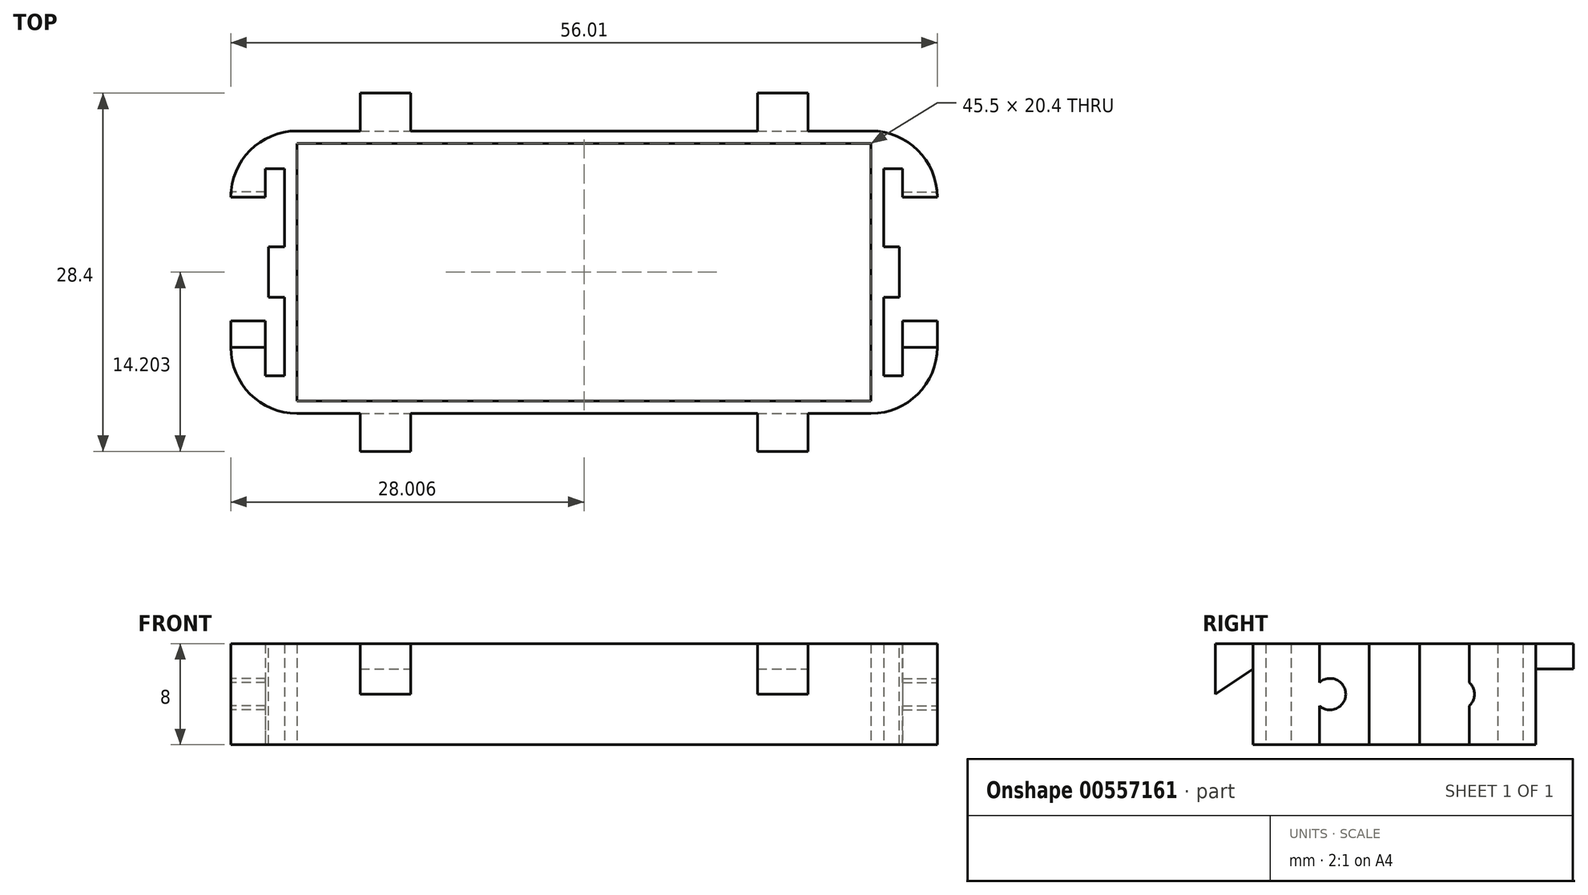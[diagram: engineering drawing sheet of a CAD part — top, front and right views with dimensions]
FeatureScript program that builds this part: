
annotation { "Feature Type Name" : "Feature", "Feature Type Description" : "" }
export const myFeature = defineFeature(function(context is Context, id is Id, definition is map)
    precondition{}
    {
        {
            var Q0;
            Q0=qCreatedBy(makeId("Top.planeOp"),FACE);
            var sketch = newSketch(context, id + "F0", { "sketchPlane" : qUnion([Q0])});
            skLineSegment(sketch, "E0.right", {"start": v(-56.91, 31.47) * mm, "end": v(-56.91, 37.67) * mm});
            skLineSegment(sketch, "E1.right", {"start": v(-58.41, 31.47) * mm, "end": v(-58.41, 37.67) * mm});
            skLineSegment(sketch, "E2", {"start": v(-58.41, 47.87) * mm, "end": v(-56.91, 47.87) * mm});
            skLineSegment(sketch, "E3", {"start": v(-58.41, 41.67) * mm, "end": v(-56.91, 41.67) * mm});
            skLineSegment(sketch, "E4.MirrorCS", {"start": v(-58.41, 31.47) * mm, "end": v(-56.91, 31.47) * mm});
            skLineSegment(sketch, "E5.MirrorCS", {"start": v(-58.41, 37.67) * mm, "end": v(-56.91, 37.67) * mm});
            skLineSegment(sketch, "E6.trimOffspring", {"start": v(-58.41, 41.67) * mm, "end": v(-58.41, 47.87) * mm});
            skLineSegment(sketch, "E7.trimOffspring", {"start": v(-56.91, 41.67) * mm, "end": v(-56.91, 47.87) * mm});
            skPoint(sketch, "E8", {"position": v(-55.91, 39.67) * mm});
            skPoint(sketch, "E9", {"position": v(-58.41, 44.77) * mm});
            skPoint(sketch, "E10", {"position": v(-58.41, 34.57) * mm});
            skPoint(sketch, "E11", {"position": v(-55.91, 50.87) * mm});
            skPoint(sketch, "E12", {"position": v(-55.91, 28.47) * mm});
            skArc(sketch, "E13", {"start": v(-55.91, 50.87) * mm, "mid": v(-59.63, 49.33) * mm, "end": v(-61.17, 45.62) * mm});
            skArc(sketch, "E14.MirrorCS", {"start": v(-55.91, 28.47) * mm, "mid": v(-59.63, 30.01) * mm, "end": v(-61.17, 33.72) * mm});
            skLineSegment(sketch, "E15", {"start": v(-61.17, 33.72) * mm, "end": v(-61.17, 45.62) * mm});
            skLineSegment(sketch, "E16.MirrorCS", {"start": v(-7.91, 37.67) * mm, "end": v(-9.41, 37.67) * mm});
            skLineSegment(sketch, "E17.MirrorCS", {"start": v(-7.91, 31.47) * mm, "end": v(-9.41, 31.47) * mm});
            skLineSegment(sketch, "E18.MirrorCS", {"start": v(-7.91, 41.67) * mm, "end": v(-9.41, 41.67) * mm});
            skLineSegment(sketch, "E19.MirrorCS", {"start": v(-7.91, 47.87) * mm, "end": v(-9.41, 47.87) * mm});
            skLineSegment(sketch, "E20.MirrorCS", {"start": v(-9.41, 31.47) * mm, "end": v(-9.41, 37.67) * mm});
            skLineSegment(sketch, "E21.MirrorCS", {"start": v(-9.41, 41.67) * mm, "end": v(-9.41, 47.87) * mm});
            skLineSegment(sketch, "E22.MirrorCS", {"start": v(-7.91, 41.67) * mm, "end": v(-7.91, 47.87) * mm});
            skLineSegment(sketch, "E23.MirrorCS", {"start": v(-7.91, 31.47) * mm, "end": v(-7.91, 37.67) * mm});
            skLineSegment(sketch, "E24.MirrorCS", {"start": v(-5.16, 33.72) * mm, "end": v(-5.16, 45.62) * mm});
            skPoint(sketch, "E25.MirrorP", {"position": v(-7.91, 34.57) * mm});
            skArc(sketch, "E26.MirrorCS", {"start": v(-10.41, 50.87) * mm, "mid": v(-6.7, 49.33) * mm, "end": v(-5.16, 45.62) * mm});
            skPoint(sketch, "E27.MirrorP", {"position": v(-10.41, 28.47) * mm});
            skPoint(sketch, "E28.MirrorP", {"position": v(-10.41, 39.67) * mm});
            skArc(sketch, "E29.MirrorCS", {"start": v(-10.41, 28.47) * mm, "mid": v(-6.7, 30.01) * mm, "end": v(-5.16, 33.72) * mm});
            skPoint(sketch, "E30.MirrorP", {"position": v(-7.91, 44.77) * mm});
            skPoint(sketch, "E31.MirrorP", {"position": v(-10.41, 50.87) * mm});
            skLineSegment(sketch, "E32", {"start": v(-55.91, 49.87) * mm, "end": v(-10.41, 49.87) * mm});
            skLineSegment(sketch, "E33", {"start": v(-55.91, 50.87) * mm, "end": v(-10.41, 50.87) * mm});
            skLineSegment(sketch, "E34", {"start": v(-55.91, 29.47) * mm, "end": v(-10.41, 29.47) * mm});
            skLineSegment(sketch, "E35", {"start": v(-55.91, 28.47) * mm, "end": v(-10.41, 28.47) * mm});
            skText(sketch, "E36", { "text": "AAA Double Holder", "fontName": "Arimo-Italic.ttf"});
            skLineSegment(sketch, "E37", {"start": v(-55.91, 49.87) * mm, "end": v(-55.91, 29.47) * mm});
            skLineSegment(sketch, "E38", {"start": v(-10.41, 49.87) * mm, "end": v(-10.41, 29.47) * mm});
            skPoint(sketch, "E39", {"position": v(-56.91, 44.77) * mm});
            skPoint(sketch, "E40", {"position": v(-61.17, 44.77) * mm});
            skPoint(sketch, "E41", {"position": v(-61.17, 34.57) * mm});
            skPoint(sketch, "E42", {"position": v(-56.91, 34.57) * mm});
            skPoint(sketch, "E43", {"position": v(-55.91, 34.57) * mm});
            skPoint(sketch, "E44", {"position": v(-55.91, 44.77) * mm});
            skPoint(sketch, "E45", {"position": v(-9.41, 44.77) * mm});
            skPoint(sketch, "E46", {"position": v(-10.41, 44.77) * mm});
            skPoint(sketch, "E47", {"position": v(-9.41, 34.57) * mm});
            skPoint(sketch, "E48", {"position": v(-10.41, 34.57) * mm});
            skPoint(sketch, "E49", {"position": v(-5.16, 34.57) * mm});
            skPoint(sketch, "E50", {"position": v(-5.16, 44.77) * mm});
            const initialGuessF0  = {"E36": [-0.0583, 0.057, 1, 0, 0.00408]};
            skSetInitialGuess(sketch, initialGuessF0);
            skSolve(sketch);
        }
        {
            var Q0;
            Q0=makeQuery(id+"F0.imprint","IMPRINT",FACE,{"disambiguationData":[TD([[makeQuery(id+"F0.imprint","IMPRINT",EDGE,{"derivedFrom":sQuery(id+"F0.wireOp",EDGE,"E0.right")}),-1.0]])]});
            extrude(context, id + "F1", {"entities" : qUnion([Q0]), "depth" : 8 * mm, "offsetDistance" : 25 * mm});
        }
        {
            var Q0;
            Q0=makeQuery(id+"F1.opExtrude","SWEPT_FACE",FACE,{"disambiguationData":[OSD([sQuery(id+"F0.wireOp",EDGE,"E24.MirrorCS")])]});
            var sketch = newSketch(context, id + "F2", { "sketchPlane" : qUnion([Q0])});
            skPoint(sketch, "E51.0", {"position": v(44.77, 0) * mm});
            skPoint(sketch, "E51.1", {"position": v(34.57, 0) * mm});
            skPoint(sketch, "E51.2", {"position": v(44.77, 0) * mm});
            skPoint(sketch, "E51.3", {"position": v(34.57, 0) * mm});
            skCircle(sketch, "E52", {"center": v(44.77, 4) * mm, "radius": 1.25 * mm});
            skPoint(sketch, "E52.centerSnap0", {"position": v(45.62, 4) * mm});
            skPoint(sketch, "E53.0", {"position": v(39.67, 0) * mm});
            skLineSegment(sketch, "E54", {"start": v(39.67, 0) * mm, "end": v(39.67, 8) * mm, "construction": true});
            skCircle(sketch, "E55.MirrorC", {"center": v(34.57, 4) * mm, "radius": 1.25 * mm});
            skSolve(sketch);
        }
        {
            var Q0;
            Q0=makeQuery(id+"F1.opExtrude","SWEPT_FACE",FACE,{"disambiguationData":[OSD([sQuery(id+"F0.wireOp",EDGE,"E15")])]});
            var sketch = newSketch(context, id + "F3", { "sketchPlane" : qUnion([Q0])});
            skPoint(sketch, "E56.0", {"position": v(-44.77, 0) * mm});
            skPoint(sketch, "E56.1", {"position": v(-34.57, 0) * mm});
            skPoint(sketch, "E56.2", {"position": v(-39.67, 0) * mm});
            skPoint(sketch, "E57.0", {"position": v(-45.62, 4) * mm});
            skPoint(sketch, "E57.1", {"position": v(-33.72, 4) * mm});
            skCircle(sketch, "E58", {"center": v(-44.77, 4) * mm, "radius": 1.25 * mm});
            skCircle(sketch, "E59.MirrorC", {"center": v(-34.57, 4) * mm, "radius": 1.25 * mm});
            skSolve(sketch);
        }
        {
            var Q0;
            {var subQ0=sQuery(id+"F3.wireOp",EDGE,"E58");var subQ1=makeQuery(id+"F1.opExtrude","SWEPT_EDGE",EDGE,{"disambiguationData":[OSD([sQuery(id+"F0.wireOp",EDGE,"E13"),sQuery(id+"F0.wireOp",EDGE,"E15")])]});var subQ2=makeQuery(id+"F3.imprint","INTERSECT",VERTEX,{"disambiguationData":[OD(0.0)],"derivedFrom":[subQ1,subQ0]});Q0=makeQuery(id+"F3.imprint","IMPRINT",FACE,{"disambiguationData":[TD([[makeQuery(id+"F3.imprint","IMPRINT",EDGE,{"disambiguationData":[TD([[subQ2,-1.0]])],"derivedFrom":subQ0}),1.0]])]});}
            var Q1;
            {var subQ0=sQuery(id+"F3.wireOp",EDGE,"E58");var subQ1=makeQuery(id+"F1.opExtrude","SWEPT_EDGE",EDGE,{"disambiguationData":[OSD([sQuery(id+"F0.wireOp",EDGE,"E13"),sQuery(id+"F0.wireOp",EDGE,"E15")])]});var subQ2=makeQuery(id+"F3.imprint","INTERSECT",VERTEX,{"disambiguationData":[OD(0.0)],"derivedFrom":[subQ1,subQ0]});Q1=makeQuery(id+"F3.imprint","IMPRINT",FACE,{"disambiguationData":[TD([[makeQuery(id+"F3.imprint","IMPRINT",EDGE,{"disambiguationData":[TD([[subQ2,1.0]])],"derivedFrom":subQ0}),1.0]])]});}
            var Q2;
            {var subQ0=sQuery(id+"F3.wireOp",EDGE,"E59.MirrorC");var subQ1=makeQuery(id+"F1.opExtrude","SWEPT_EDGE",EDGE,{"disambiguationData":[OSD([sQuery(id+"F0.wireOp",EDGE,"E14.MirrorCS"),sQuery(id+"F0.wireOp",EDGE,"E15")])]});var subQ2=makeQuery(id+"F3.imprint","INTERSECT",VERTEX,{"disambiguationData":[OD(0.0)],"derivedFrom":[subQ1,subQ0]});Q2=makeQuery(id+"F3.imprint","IMPRINT",FACE,{"disambiguationData":[TD([[makeQuery(id+"F3.imprint","IMPRINT",EDGE,{"disambiguationData":[TD([[subQ2,-1.0]])],"derivedFrom":subQ0}),-1.0]])]});}
            var Q3;
            {var subQ0=sQuery(id+"F3.wireOp",EDGE,"E59.MirrorC");var subQ1=makeQuery(id+"F1.opExtrude","SWEPT_EDGE",EDGE,{"disambiguationData":[OSD([sQuery(id+"F0.wireOp",EDGE,"E14.MirrorCS"),sQuery(id+"F0.wireOp",EDGE,"E15")])]});var subQ2=makeQuery(id+"F3.imprint","INTERSECT",VERTEX,{"disambiguationData":[OD(0.0)],"derivedFrom":[subQ1,subQ0]});Q3=makeQuery(id+"F3.imprint","IMPRINT",FACE,{"disambiguationData":[TD([[makeQuery(id+"F3.imprint","IMPRINT",EDGE,{"disambiguationData":[TD([[subQ2,1.0]])],"derivedFrom":subQ0}),-1.0]])]});}
            extrude(context, id + "F4", {"entities" : qUnion([Q0, Q1, Q2, Q3]), "operationType" : NewBodyOperationType.REMOVE, "oppositeDirection" : true, "depth" : 3 * mm, "offsetDistance" : 25 * mm});
        }
        {
            var Q0;
            {var subQ0=sQuery(id+"F2.wireOp",EDGE,"E55.MirrorC");var subQ1=makeQuery(id+"F1.opExtrude","SWEPT_EDGE",EDGE,{"disambiguationData":[OSD([sQuery(id+"F0.wireOp",EDGE,"E24.MirrorCS"),sQuery(id+"F0.wireOp",EDGE,"E29.MirrorCS")])]});var subQ2=makeQuery(id+"F2.imprint","INTERSECT",VERTEX,{"disambiguationData":[OD(0.0)],"derivedFrom":[subQ1,subQ0]});Q0=makeQuery(id+"F2.imprint","IMPRINT",FACE,{"disambiguationData":[TD([[makeQuery(id+"F2.imprint","IMPRINT",EDGE,{"disambiguationData":[TD([[subQ2,1.0]])],"derivedFrom":subQ0}),-1.0]])]});}
            var Q1;
            {var subQ0=sQuery(id+"F2.wireOp",EDGE,"E52");var subQ1=makeQuery(id+"F1.opExtrude","SWEPT_EDGE",EDGE,{"disambiguationData":[OSD([sQuery(id+"F0.wireOp",EDGE,"E24.MirrorCS"),sQuery(id+"F0.wireOp",EDGE,"E26.MirrorCS")])]});var subQ2=makeQuery(id+"F2.imprint","INTERSECT",VERTEX,{"disambiguationData":[OD(0.0)],"derivedFrom":[subQ1,subQ0]});Q1=makeQuery(id+"F2.imprint","IMPRINT",FACE,{"disambiguationData":[TD([[makeQuery(id+"F2.imprint","IMPRINT",EDGE,{"disambiguationData":[TD([[subQ2,1.0]])],"derivedFrom":subQ0}),1.0]])]});}
            var Q2;
            {var subQ0=sQuery(id+"F2.wireOp",EDGE,"E52");var subQ1=makeQuery(id+"F1.opExtrude","SWEPT_EDGE",EDGE,{"disambiguationData":[OSD([sQuery(id+"F0.wireOp",EDGE,"E24.MirrorCS"),sQuery(id+"F0.wireOp",EDGE,"E26.MirrorCS")])]});var subQ2=makeQuery(id+"F2.imprint","INTERSECT",VERTEX,{"disambiguationData":[OD(0.0)],"derivedFrom":[subQ1,subQ0]});Q2=makeQuery(id+"F2.imprint","IMPRINT",FACE,{"disambiguationData":[TD([[makeQuery(id+"F2.imprint","IMPRINT",EDGE,{"disambiguationData":[TD([[subQ2,-1.0]])],"derivedFrom":subQ0}),1.0]])]});}
            var Q3;
            {var subQ0=sQuery(id+"F2.wireOp",EDGE,"E55.MirrorC");var subQ1=makeQuery(id+"F1.opExtrude","SWEPT_EDGE",EDGE,{"disambiguationData":[OSD([sQuery(id+"F0.wireOp",EDGE,"E24.MirrorCS"),sQuery(id+"F0.wireOp",EDGE,"E29.MirrorCS")])]});var subQ2=makeQuery(id+"F2.imprint","INTERSECT",VERTEX,{"disambiguationData":[OD(0.0)],"derivedFrom":[subQ1,subQ0]});Q3=makeQuery(id+"F2.imprint","IMPRINT",FACE,{"disambiguationData":[TD([[makeQuery(id+"F2.imprint","IMPRINT",EDGE,{"disambiguationData":[TD([[subQ2,-1.0]])],"derivedFrom":subQ0}),-1.0]])]});}
            extrude(context, id + "F5", {"entities" : qUnion([Q0, Q1, Q2, Q3]), "operationType" : NewBodyOperationType.REMOVE, "oppositeDirection" : true, "depth" : 3 * mm, "offsetDistance" : 25 * mm});
        }
        {
            var Q0;
            Q0=makeQuery(id+"F1.opExtrude","CAP_FACE",FACE,{"disambiguationData":[OSD([sQuery(id+"F0.wireOp",EDGE,"E0.right"),sQuery(id+"F0.wireOp",EDGE,"E1.right"),sQuery(id+"F0.wireOp",EDGE,"E2"),sQuery(id+"F0.wireOp",EDGE,"E3"),sQuery(id+"F0.wireOp",EDGE,"E4.MirrorCS"),sQuery(id+"F0.wireOp",EDGE,"E5.MirrorCS"),sQuery(id+"F0.wireOp",EDGE,"E6.trimOffspring"),sQuery(id+"F0.wireOp",EDGE,"E7.trimOffspring"),sQuery(id+"F0.wireOp",EDGE,"E13"),sQuery(id+"F0.wireOp",EDGE,"E14.MirrorCS"),sQuery(id+"F0.wireOp",EDGE,"E15"),sQuery(id+"F0.wireOp",EDGE,"E16.MirrorCS"),sQuery(id+"F0.wireOp",EDGE,"E17.MirrorCS"),sQuery(id+"F0.wireOp",EDGE,"E18.MirrorCS"),sQuery(id+"F0.wireOp",EDGE,"E19.MirrorCS"),sQuery(id+"F0.wireOp",EDGE,"E22.MirrorCS"),sQuery(id+"F0.wireOp",EDGE,"E23.MirrorCS"),sQuery(id+"F0.wireOp",EDGE,"E20.MirrorCS"),sQuery(id+"F0.wireOp",EDGE,"E21.MirrorCS"),sQuery(id+"F0.wireOp",EDGE,"E24.MirrorCS"),sQuery(id+"F0.wireOp",EDGE,"E26.MirrorCS"),sQuery(id+"F0.wireOp",EDGE,"E29.MirrorCS"),sQuery(id+"F0.wireOp",EDGE,"E32"),sQuery(id+"F0.wireOp",EDGE,"E33"),sQuery(id+"F0.wireOp",EDGE,"E34"),sQuery(id+"F0.wireOp",EDGE,"E35"),sQuery(id+"F0.wireOp",EDGE,"E37"),sQuery(id+"F0.wireOp",EDGE,"E38")])],"isStart":false});
            var sketch = newSketch(context, id + "F6", { "sketchPlane" : qUnion([Q0])});
            skPoint(sketch, "E60", {"position": v(-33.16, 50.87) * mm});
            skLineSegment(sketch, "E61", {"start": v(-55.91, 39.67) * mm, "end": v(-10.41, 39.67) * mm, "construction": true});
            skPoint(sketch, "E62.0", {"position": v(-55.91, 50.87) * mm});
            skPoint(sketch, "E62.1", {"position": v(-10.41, 50.87) * mm});
            skPoint(sketch, "E63.0", {"position": v(-55.91, 28.47) * mm});
            skPoint(sketch, "E63.1", {"position": v(-10.41, 28.47) * mm});
            skPoint(sketch, "E64", {"position": v(-33.16, 28.47) * mm});
            skPoint(sketch, "E65", {"position": v(-17.41, 50.87) * mm});
            skPoint(sketch, "E66", {"position": v(-48.91, 50.87) * mm});
            skPoint(sketch, "E67", {"position": v(-48.91, 28.47) * mm});
            skPoint(sketch, "E68", {"position": v(-17.41, 28.47) * mm});
            skLineSegment(sketch, "E69", {"start": v(-19.41, 53.87) * mm, "end": v(-19.41, 50.87) * mm});
            skLineSegment(sketch, "E70", {"start": v(-15.41, 53.87) * mm, "end": v(-15.41, 50.87) * mm});
            skLineSegment(sketch, "E71", {"start": v(-19.41, 53.87) * mm, "end": v(-15.41, 53.87) * mm});
            skLineSegment(sketch, "E72.MirrorCS", {"start": v(-15.41, 25.47) * mm, "end": v(-15.41, 28.47) * mm});
            skLineSegment(sketch, "E73.MirrorCS", {"start": v(-19.41, 25.47) * mm, "end": v(-19.41, 28.47) * mm});
            skLineSegment(sketch, "E74.MirrorCS", {"start": v(-19.41, 25.47) * mm, "end": v(-15.41, 25.47) * mm});
            skLineSegment(sketch, "E75", {"start": v(-33.16, 50.87) * mm, "end": v(-33.16, 28.47) * mm, "construction": true});
            skLineSegment(sketch, "E76.MirrorCS", {"start": v(-46.91, 53.87) * mm, "end": v(-46.91, 50.87) * mm});
            skLineSegment(sketch, "E77.MirrorCS", {"start": v(-46.91, 53.87) * mm, "end": v(-50.91, 53.87) * mm});
            skLineSegment(sketch, "E78.MirrorCS", {"start": v(-50.91, 53.87) * mm, "end": v(-50.91, 50.87) * mm});
            skLineSegment(sketch, "E79.MirrorCS", {"start": v(-50.91, 25.47) * mm, "end": v(-50.91, 28.47) * mm});
            skLineSegment(sketch, "E80.MirrorCS", {"start": v(-46.91, 25.47) * mm, "end": v(-50.91, 25.47) * mm});
            skLineSegment(sketch, "E81.MirrorCS", {"start": v(-46.91, 25.47) * mm, "end": v(-46.91, 28.47) * mm});
            skSolve(sketch);
        }
        {
            var Q0;
            {var subQ0=sQuery(id+"F6.wireOp",EDGE,"E69");Q0=makeQuery(id+"F6.imprint","IMPRINT",FACE,{"disambiguationData":[TD([[makeQuery(id+"F6.imprint","IMPRINT",EDGE,{"derivedFrom":subQ0}),1.0]])]});}
            var Q1;
            {var subQ0=sQuery(id+"F6.wireOp",EDGE,"E76.MirrorCS");Q1=makeQuery(id+"F6.imprint","IMPRINT",FACE,{"disambiguationData":[TD([[makeQuery(id+"F6.imprint","IMPRINT",EDGE,{"derivedFrom":subQ0}),-1.0]])]});}
            var Q2;
            {var subQ0=sQuery(id+"F6.wireOp",EDGE,"E79.MirrorCS");Q2=makeQuery(id+"F6.imprint","IMPRINT",FACE,{"disambiguationData":[TD([[makeQuery(id+"F6.imprint","IMPRINT",EDGE,{"derivedFrom":subQ0}),-1.0]])]});}
            var Q3;
            {var subQ0=sQuery(id+"F6.wireOp",EDGE,"E72.MirrorCS");Q3=makeQuery(id+"F6.imprint","IMPRINT",FACE,{"disambiguationData":[TD([[makeQuery(id+"F6.imprint","IMPRINT",EDGE,{"derivedFrom":subQ0}),1.0]])]});}
            extrude(context, id + "F7", {"entities" : qUnion([Q0, Q1, Q2, Q3]), "operationType" : NewBodyOperationType.ADD, "oppositeDirection" : true, "depth" : 2 * mm, "offsetDistance" : 25 * mm});
        }
        {
            var Q0;
            Q0=makeQuery(id+"F7.opExtrude","SWEPT_FACE",FACE,{"disambiguationData":[OSD([sQuery(id+"F6.wireOp",EDGE,"E72.MirrorCS")])]});
            var sketch = newSketch(context, id + "F8", { "sketchPlane" : qUnion([Q0])});
            skLineSegment(sketch, "E82.0", {"start": v(25.47, 6) * mm, "end": v(28.47, 6) * mm});
            skLineSegment(sketch, "E82.1", {"start": v(28.47, 6) * mm, "end": v(28.47, 8) * mm});
            skLineSegment(sketch, "E82.2", {"start": v(25.47, 8) * mm, "end": v(28.47, 8) * mm});
            skLineSegment(sketch, "E82.3", {"start": v(25.47, 6) * mm, "end": v(25.47, 8) * mm});
            skLineSegment(sketch, "E83", {"start": v(25.47, 6) * mm, "end": v(25.47, 4) * mm});
            skLineSegment(sketch, "E84", {"start": v(25.47, 4) * mm, "end": v(28.47, 6) * mm});
            skSolve(sketch);
        }
        {
            var Q0;
            Q0=makeQuery(id+"F7.opExtrude","SWEPT_FACE",FACE,{"disambiguationData":[OSD([sQuery(id+"F6.wireOp",EDGE,"E79.MirrorCS")])]});
            var sketch = newSketch(context, id + "F9", { "sketchPlane" : qUnion([Q0])});
            skPoint(sketch, "E85", {"position": v(-25.47, 4) * mm});
            skLineSegment(sketch, "E86", {"start": v(-25.47, 4) * mm, "end": v(-25.47, 6) * mm});
            skLineSegment(sketch, "E87", {"start": v(-25.47, 4) * mm, "end": v(-28.47, 6) * mm});
            skSolve(sketch);
        }
        {
            var Q0;
            Q0=sQuery(id+"F6.wireOp",EDGE,"E61");
            cPlane(context, id + "F10", {"entities" : qUnion([Q0]), "cplaneType" : CPlaneType.LINE_ANGLE, "offset" : 25 * mm, "angle" : 0 * degree, "width" : 150 * mm, "height" : 150 * mm});
        }
        {
            var Q0;
            Q0=makeQuery(id+"F8.imprint","IMPRINT",FACE,{"disambiguationData":[TD([[makeQuery(id+"F8.imprint","IMPRINT",EDGE,{"derivedFrom":sQuery(id+"F8.wireOp",EDGE,"E82.0")}),-1.0]])]});
            extrude(context, id + "F11", {"entities" : qUnion([Q0]), "operationType" : NewBodyOperationType.ADD, "oppositeDirection" : true, "depth" : 4 * mm, "offsetDistance" : 25 * mm});
        }
        {
            var Q0;
            Q0=makeQuery(id+"F9.imprint","IMPRINT",FACE,{"disambiguationData":[TD([[makeQuery(id+"F9.imprint","IMPRINT",EDGE,{"derivedFrom":sQuery(id+"F9.wireOp",EDGE,"E86")}),1.0]])]});
            extrude(context, id + "F12", {"entities" : qUnion([Q0]), "operationType" : NewBodyOperationType.ADD, "oppositeDirection" : true, "depth" : 4 * mm, "offsetDistance" : 25 * mm});
        }
    });
